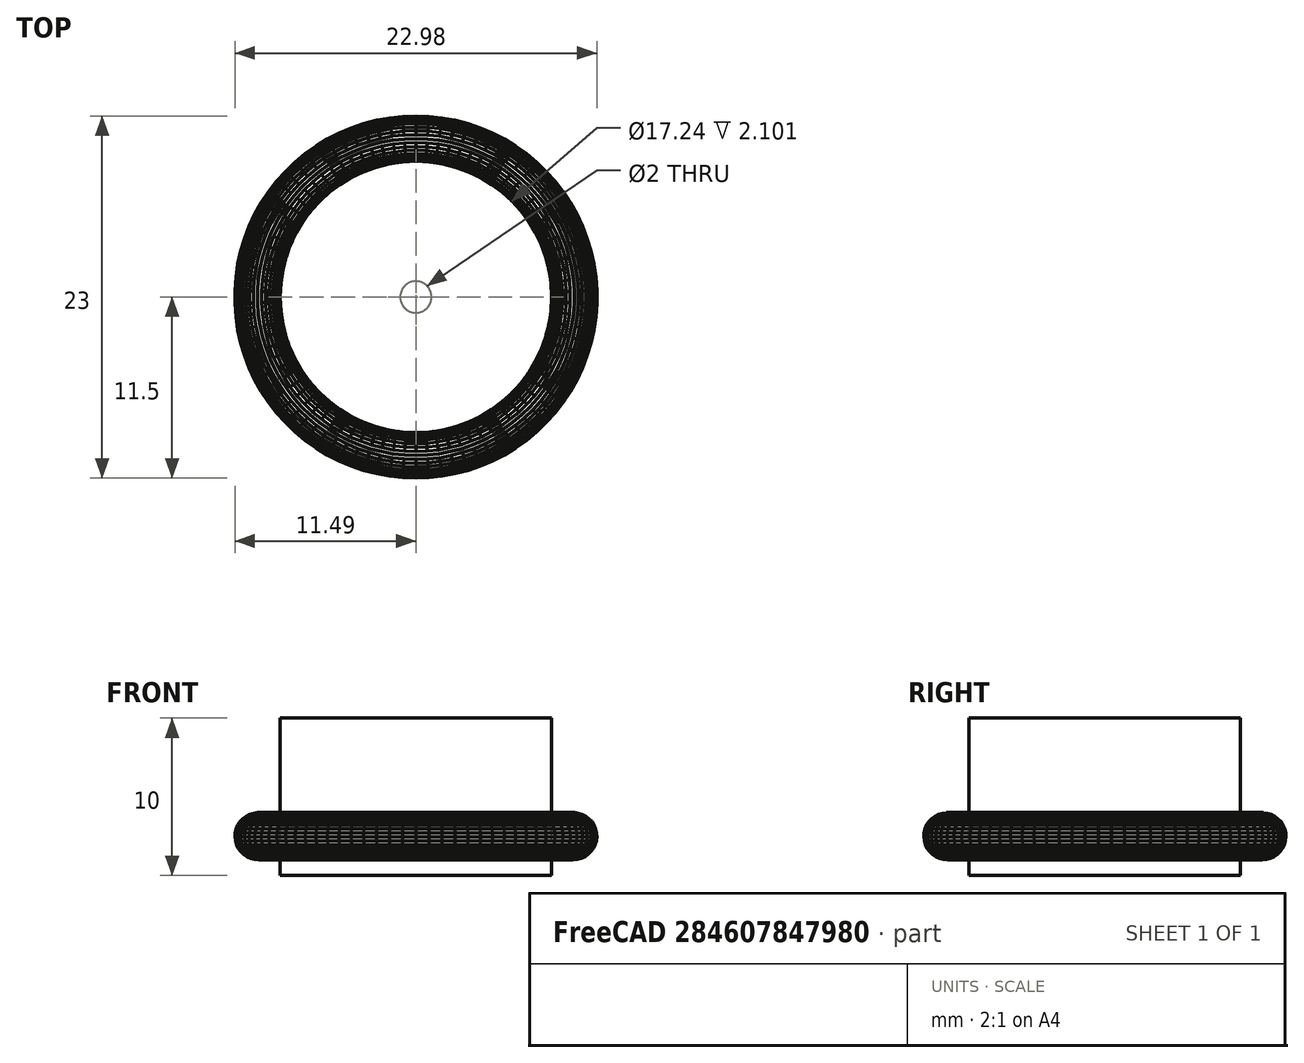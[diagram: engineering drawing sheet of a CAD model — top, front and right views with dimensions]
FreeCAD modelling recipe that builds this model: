
FCSTD DOCUMENT  (FreeCAD 0.18.3R)
Label: Wheel and Tire
License: All rights reserved
LicenseURL: http://en.wikipedia.org/wiki/All_rights_reserved
objects: Part::FeaturePython×3, Part::Feature×2, Part::Cylinder×2, Mesh::Feature×1, Part::Cut×1, App::DocumentObjectGroup×1
note: 8 computed .brp shape members not serialized (recipe doc carries the construction recipe); baked Part::Feature solids carry a one-line shape summary decoded from their .brp

FEATURE [Mesh::Feature] Wheel_and_Tire  label="Wheel and Tire"
FEATURE [Part::Feature] Wheel_and_Tire001
  Placement = pos=(0,0,0) rot=(1,0,0;1.5708rad)
  shape: bbox 22.98 x 23 x 2.998 mm, 4828 faces, 0 solids (baked)
FEATURE [Part::Cylinder] Cylinder002
  Angle = 360
  AttacherType = Attacher::AttachEngine3D
  Height = 10
  Placement = pos=(11.5,-11.5,0) rot=(0,0,1;0rad)
  Radius = 1
FEATURE [Part::Feature] Solid
  shape: bbox 22.98 x 23 x 2.998 mm, 4477 faces (baked)
FEATURE [Part::Cut] Cut
  Base = -> Solid
  Tool = -> Cylinder002
FEATURE [Part::Cylinder] Cylinder001
  Angle = 360
  AttacherType = Attacher::AttachEngine3D
  Height = 10
  Placement = pos=(11.5,-11.5,-1) rot=(0,0,1;0rad)
  Radius = 8.62
FEATURE [Part::FeaturePython] Slice  # WARN: FeaturePython — macro-defined, semantics opaque (R4)
  Base = -> Cut
  Mode = 1
  Tolerance = 0
  Tools = -> [Cylinder001]
FEATURE [Part::FeaturePython] Slice_child0  label="Tire"  # WARN: FeaturePython — macro-defined, semantics opaque (R4)
  Base = -> Slice
  FilterType = 1
  Invert = false
  OverrideMaxVal = 0
  WindowFrom = 80
  WindowTo = 100
  items = 0
FEATURE [Part::FeaturePython] Slice_child1  label="Wheel"  # WARN: FeaturePython — macro-defined, semantics opaque (R4)
  Base = -> Slice
  FilterType = 1
  Invert = false
  OverrideMaxVal = 0
  WindowFrom = 80
  WindowTo = 100
  items = 1
FEATURE [App::DocumentObjectGroup] GrExplode_Slice  label="Exploded Slice"
  Group = -> [Slice_child0,Slice_child1]
